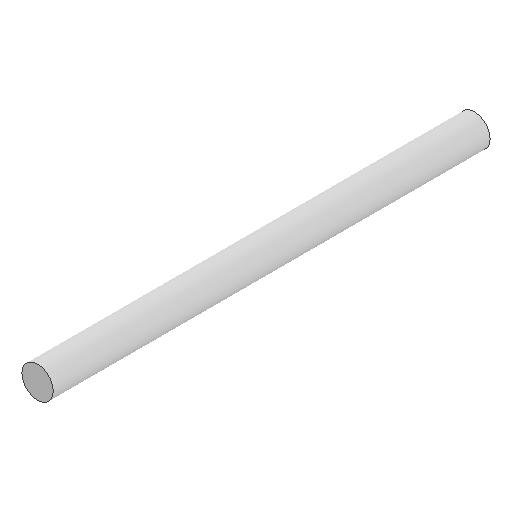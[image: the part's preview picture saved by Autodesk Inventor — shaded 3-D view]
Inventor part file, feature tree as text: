
AUTODESK INVENTOR PART (.ipt)
format: ipt  version: 2025.1 (Build 291241000, 241)  size: 79,872 bytes
history: native  units: mm
features: other x1, extrude x1, sketch x1
ambient origin geometry x8: Origin, YZ Plane, XZ Plane, XY Plane, X Axis, Y Axis, Z Axis, Center Point
bodies: Body1 (feature_tree)
feature tree (3):
  other  "Bryła1"
  extrude  "Wyciągnięcie proste1"  Depth=5.0mm
  sketch  "Szkic1"
